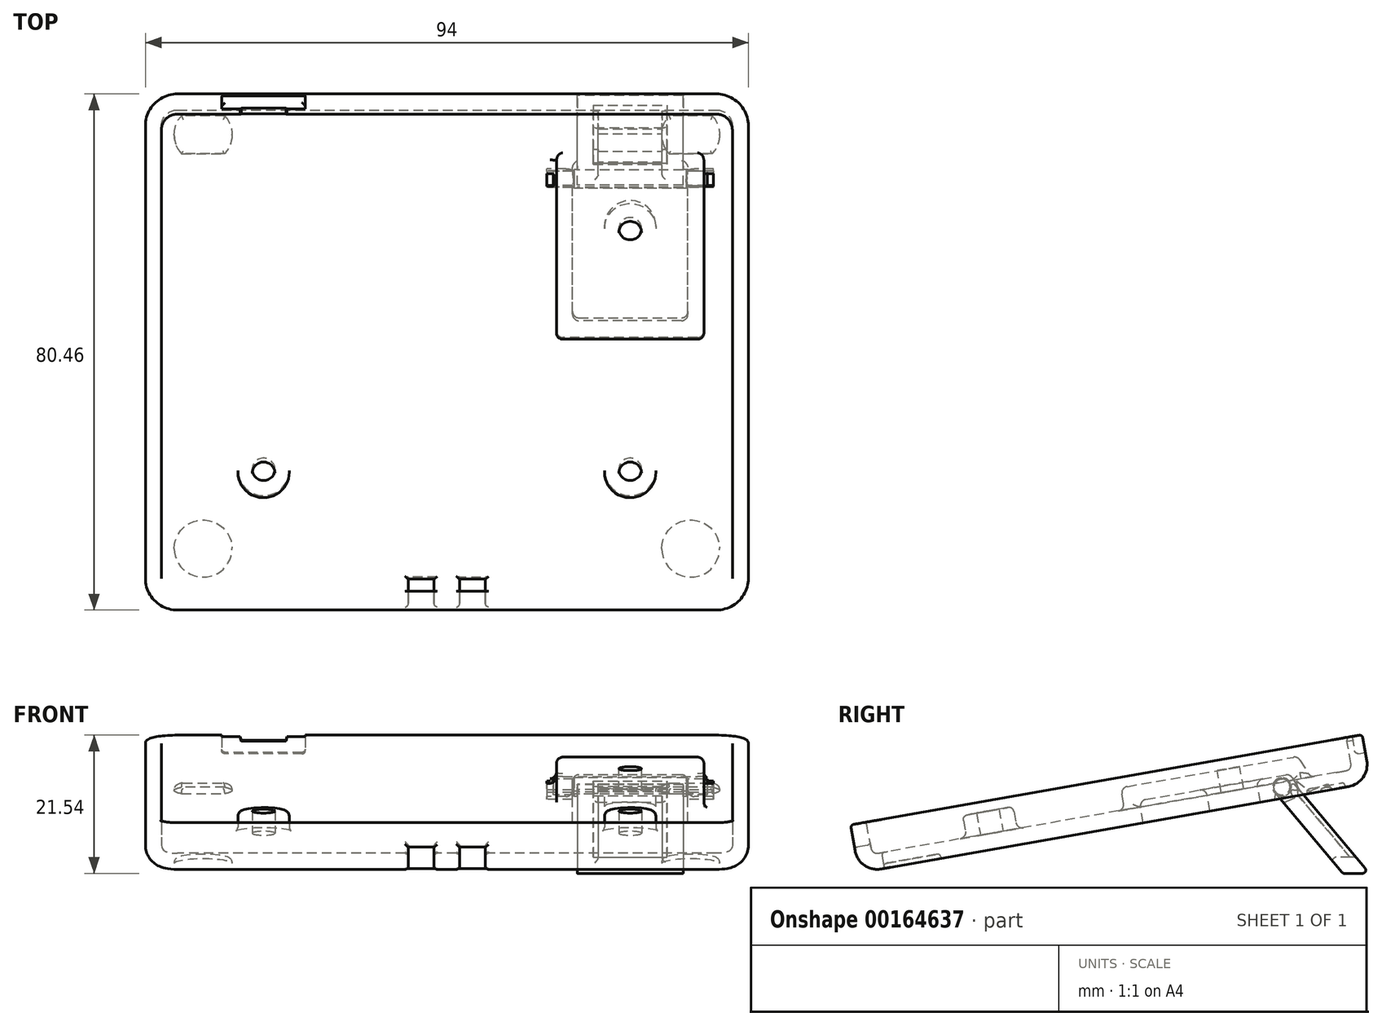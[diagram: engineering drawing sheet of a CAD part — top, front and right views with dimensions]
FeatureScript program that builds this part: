
annotation { "Feature Type Name" : "Feature", "Feature Type Description" : "" }
export const myFeature = defineFeature(function(context is Context, id is Id, definition is map)
    precondition{}
    {
        {
            var Q0;
            Q0=qCreatedBy(makeId("Top.planeOp"),FACE);
            var sketch = newSketch(context, id + "F0", { "sketchPlane" : qUnion([Q0])});
            skLineSegment(sketch, "E0.bottom", {"start": v(-47, 40.5) * mm, "end": v(47, 40.5) * mm});
            skLineSegment(sketch, "E0.top", {"start": v(-47, -40.5) * mm, "end": v(47, -40.5) * mm});
            skLineSegment(sketch, "E0.left", {"start": v(-47, 40.5) * mm, "end": v(-47, -40.5) * mm});
            skLineSegment(sketch, "E0.right", {"start": v(47, 40.5) * mm, "end": v(47, -40.5) * mm});
            skPoint(sketch, "E1", {"position": v(0, -40.5) * mm});
            skSolve(sketch);
        }
        {
            var Q0;
            Q0=qSketchRegion(id+"F0",true);
            extrude(context, id + "F1", {"entities" : qUnion([Q0]), "depth" : 7.6 * mm});
        }
        {
            var Q0;
            Q0=makeQuery(id+"F1.opExtrude","SWEPT_EDGE",EDGE,{"disambiguationData":[OSD([sQuery(id+"F0.wireOp",EDGE,"E0.top"),sQuery(id+"F0.wireOp",EDGE,"E0.left")])]});
            var Q1;
            Q1=makeQuery(id+"F1.opExtrude","SWEPT_EDGE",EDGE,{"disambiguationData":[OSD([sQuery(id+"F0.wireOp",EDGE,"E0.bottom"),sQuery(id+"F0.wireOp",EDGE,"E0.left")])]});
            var Q2;
            Q2=makeQuery(id+"F1.opExtrude","SWEPT_EDGE",EDGE,{"disambiguationData":[OSD([sQuery(id+"F0.wireOp",EDGE,"E0.top"),sQuery(id+"F0.wireOp",EDGE,"E0.right")])]});
            var Q3;
            Q3=makeQuery(id+"F1.opExtrude","SWEPT_EDGE",EDGE,{"disambiguationData":[OSD([sQuery(id+"F0.wireOp",EDGE,"E0.bottom"),sQuery(id+"F0.wireOp",EDGE,"E0.right")])]});
            fillet(context, id + "F2", {"entities" : qUnion([Q0, Q1, Q2, Q3]), "radius" : 5 * mm, "tangentPropagation" : true, "allowEdgeOverflow" : false});
        }
        {
            assignVariable(context, id + "F3", {"name" : "Thickness", "anyValue" : 2.5});
        }
        {
            var Q0;
            Q0=makeQuery(id+"F1.opExtrude","CAP_FACE",FACE,{"disambiguationData":[OSD([sQuery(id+"F0.wireOp",EDGE,"E0.bottom"),sQuery(id+"F0.wireOp",EDGE,"E0.top"),sQuery(id+"F0.wireOp",EDGE,"E0.left"),sQuery(id+"F0.wireOp",EDGE,"E0.right")])],"isStart":false});
            shell(context, id + "F4", {"entities" : qUnion([Q0]), "thickness" : (getVariable(context, 'Thickness')) * mm});
        }
        {
            var Q0;
            Q0=makeQuery(id+"F4.opShell","OFFSET_FACE",FACE,{"disambiguationData":[OSD([sQuery(id+"F0.wireOp",EDGE,"E0.bottom"),sQuery(id+"F0.wireOp",EDGE,"E0.top"),sQuery(id+"F0.wireOp",EDGE,"E0.left"),sQuery(id+"F0.wireOp",EDGE,"E0.right")])]});
            var sketch = newSketch(context, id + "F5", { "sketchPlane" : qUnion([Q0])});
            skCircle(sketch, "E2", {"center": v(-28.57, -19.05) * mm, "radius": 4 * mm});
            skCircle(sketch, "E3.0.1.0", {"center": v(-28.57, 19.05) * mm, "radius": 4 * mm, "construction": true});
            skCircle(sketch, "E3.1.0.0", {"center": v(28.58, -19.05) * mm, "radius": 4 * mm});
            skCircle(sketch, "E3.1.1.0", {"center": v(28.58, 19.05) * mm, "radius": 4 * mm, "construction": true});
            skLineSegment(sketch, "E3.direction1", {"start": v(-28.57, -19.05) * mm, "end": v(28.58, -19.05) * mm, "construction": true});
            skLineSegment(sketch, "E3.direction2", {"start": v(-28.57, -19.05) * mm, "end": v(-28.57, 19.05) * mm, "construction": true});
            skSolve(sketch);
        }
        {
            var Q0;
            Q0=qSketchRegion(id+"F5",true);
            extrude(context, id + "F6", {"entities" : qUnion([Q0]), "operationType" : NewBodyOperationType.ADD, "depth" : 3.5 * mm});
        }
        {
            var Q0;
            Q0=makeQuery(id+"F5.imprint","IMPRINT",FACE,{"disambiguationData":[TD([[makeQuery(id+"F5.imprint","IMPRINT",EDGE,{"derivedFrom":sQuery(id+"F5.wireOp",EDGE,"E2")}),-1.0]])]});
            var sketch = newSketch(context, id + "F7", { "sketchPlane" : qUnion([Q0])});
            skCircle(sketch, "E4", {"center": v(-28.57, -19.05) * mm, "radius": 1.77 * mm});
            skCircle(sketch, "E5.0.1.0", {"center": v(-28.57, 19.05) * mm, "radius": 1.77 * mm});
            skCircle(sketch, "E5.1.0.0", {"center": v(28.58, -19.05) * mm, "radius": 1.77 * mm});
            skCircle(sketch, "E5.1.1.0", {"center": v(28.58, 19.05) * mm, "radius": 1.77 * mm});
            skLineSegment(sketch, "E5.direction1", {"start": v(-28.57, -19.05) * mm, "end": v(28.58, -19.05) * mm, "construction": true});
            skLineSegment(sketch, "E5.direction2", {"start": v(-28.57, -19.05) * mm, "end": v(-28.57, 19.05) * mm, "construction": true});
            skSolve(sketch);
        }
        {
            var Q0;
            Q0=qSketchRegion(id+"F7",true);
            extrude(context, id + "F8", {"entities" : qUnion([Q0]), "operationType" : NewBodyOperationType.REMOVE, "depth" : 25 * mm});
        }
        {
            var Q0;
            Q0=makeQuery(id+"F6.opExtrude","CAP_EDGE",EDGE,{"disambiguationData":[OSD([sQuery(id+"F5.wireOp",EDGE,"E3.0.1.0")])],"isStart":false});
            var Q1;
            Q1=makeQuery(id+"F6.opExtrude","CAP_EDGE",EDGE,{"disambiguationData":[OSD([sQuery(id+"F5.wireOp",EDGE,"E2")])],"isStart":false});
            var Q2;
            Q2=makeQuery(id+"F6.opExtrude","CAP_EDGE",EDGE,{"disambiguationData":[OSD([sQuery(id+"F5.wireOp",EDGE,"E3.1.1.0")])],"isStart":false});
            var Q3;
            Q3=makeQuery(id+"F6.opExtrude","CAP_EDGE",EDGE,{"disambiguationData":[OSD([sQuery(id+"F5.wireOp",EDGE,"E3.1.0.0")])],"isStart":false});
            fillet(context, id + "F9", {"entities" : qUnion([Q0, Q1, Q2, Q3]), "radius" : 0.8 * mm, "tangentPropagation" : true, "allowEdgeOverflow" : false});
        }
        {
            var Q0;
            Q0=makeQuery(id+"F4.opShell","OFFSET_FACE",FACE,{"disambiguationData":[OSD([sQuery(id+"F0.wireOp",EDGE,"E0.bottom"),sQuery(id+"F0.wireOp",EDGE,"E0.top"),sQuery(id+"F0.wireOp",EDGE,"E0.left"),sQuery(id+"F0.wireOp",EDGE,"E0.right")])]});
            fillet(context, id + "F10", {"entities" : qUnion([Q0]), "radius" : 1 * mm, "tangentPropagation" : true, "allowEdgeOverflow" : false});
        }
        {
            var Q0;
            Q0=makeQuery(id+"F1.opExtrude","CAP_FACE",FACE,{"disambiguationData":[OSD([sQuery(id+"F0.wireOp",EDGE,"E0.bottom"),sQuery(id+"F0.wireOp",EDGE,"E0.top"),sQuery(id+"F0.wireOp",EDGE,"E0.left"),sQuery(id+"F0.wireOp",EDGE,"E0.right")])],"isStart":true});
            fillet(context, id + "F11", {"entities" : qUnion([Q0]), "radius" : 3.5 * mm, "tangentPropagation" : true, "allowEdgeOverflow" : false});
        }
        {
            var Q0;
            Q0=makeQuery(id+"F1.opExtrude","CAP_FACE",FACE,{"disambiguationData":[OSD([sQuery(id+"F0.wireOp",EDGE,"E0.bottom"),sQuery(id+"F0.wireOp",EDGE,"E0.top"),sQuery(id+"F0.wireOp",EDGE,"E0.left"),sQuery(id+"F0.wireOp",EDGE,"E0.right")])],"isStart":true});
            var sketch = newSketch(context, id + "F12", { "sketchPlane" : qUnion([Q0])});
            skLineSegment(sketch, "E6", {"start": v(0, 29.34) * mm, "end": v(0, 8.5) * mm, "construction": true});
            skCircle(sketch, "E7", {"center": v(-38, 32) * mm, "radius": 4.5 * mm});
            skCircle(sketch, "E8.MirrorC", {"center": v(38, 32) * mm, "radius": 4.5 * mm});
            skLineSegment(sketch, "E9.direction1", {"start": v(-38, 32) * mm, "end": v(-13, 32) * mm, "construction": true});
            skCircle(sketch, "E10.0.1.0", {"center": v(-38, -33.5) * mm, "radius": 4.5 * mm, "construction": true});
            skLineSegment(sketch, "E10.direction2", {"start": v(-38, 32) * mm, "end": v(-38, -33.5) * mm, "construction": true});
            skCircle(sketch, "E11.0.1.0", {"center": v(38, -32) * mm, "radius": 4.5 * mm, "construction": true});
            skLineSegment(sketch, "E11.direction1", {"start": v(38, 32) * mm, "end": v(63, 32) * mm, "construction": true});
            skLineSegment(sketch, "E11.direction2", {"start": v(38, 32) * mm, "end": v(38, -32) * mm, "construction": true});
            skLineSegment(sketch, "E12", {"start": v(-41.35, -30.5) * mm, "end": v(-34.65, -30.5) * mm});
            skLineSegment(sketch, "E13", {"start": v(-34.65, -36.5) * mm, "end": v(-41.35, -36.5) * mm});
            skLineSegment(sketch, "E14", {"start": v(-38, -33.5) * mm, "end": v(-34.31, -33.5) * mm, "construction": true});
            skArc(sketch, "E15", {"start": v(-34.65, -36.5) * mm, "mid": v(-33.5, -33.5) * mm, "end": v(-34.65, -30.5) * mm});
            skArc(sketch, "E16", {"start": v(-41.35, -30.5) * mm, "mid": v(-42.5, -33.5) * mm, "end": v(-41.35, -36.5) * mm});
            skLineSegment(sketch, "E17.1.0.0", {"start": v(41.35, -36.5) * mm, "end": v(34.65, -36.5) * mm});
            skArc(sketch, "E17.1.0.1", {"start": v(41.35, -36.5) * mm, "mid": v(42.5, -33.5) * mm, "end": v(41.35, -30.5) * mm});
            skArc(sketch, "E17.1.0.2", {"start": v(34.65, -30.5) * mm, "mid": v(33.5, -33.5) * mm, "end": v(34.65, -36.5) * mm});
            skLineSegment(sketch, "E17.1.0.3", {"start": v(34.65, -30.5) * mm, "end": v(41.35, -30.5) * mm});
            skLineSegment(sketch, "E17.direction1", {"start": v(-41.35, -36.5) * mm, "end": v(34.65, -36.5) * mm, "construction": true});
            skSolve(sketch);
        }
        {
            var Q0;
            Q0=makeQuery(id+"F1.opExtrude","CAP_FACE",FACE,{"disambiguationData":[OSD([sQuery(id+"F0.wireOp",EDGE,"E0.bottom"),sQuery(id+"F0.wireOp",EDGE,"E0.top"),sQuery(id+"F0.wireOp",EDGE,"E0.left"),sQuery(id+"F0.wireOp",EDGE,"E0.right")])],"isStart":false});
            fillet(context, id + "F13", {"entities" : qUnion([Q0]), "radius" : 0.5 * mm, "tangentPropagation" : true, "allowEdgeOverflow" : false});
        }
        {
            var Q0;
            Q0=qCreatedBy(makeId("Top.planeOp"),FACE);
            var sketch = newSketch(context, id + "F14", { "sketchPlane" : qUnion([Q0])});
            skLineSegment(sketch, "E18", {"start": v(-15.25, 0) * mm, "end": v(18.86, 0) * mm});
            skSolve(sketch);
        }
        {
            assignVariable(context, id + "F15", {"name" : "FootWidth", "anyValue" : 23});
        }
        {
            var Q0;
            Q0=qCreatedBy(makeId("Right.planeOp"),FACE);
            cPlane(context, id + "F16", {"entities" : qUnion([Q0]), "cplaneType" : CPlaneType.OFFSET, "offset" : 28.57 * mm, "width" : 150 * mm, "height" : 150 * mm});
        }
        {
            var Q0;
            Q0=qCreatedBy(id+"F16.planeOp",FACE);
            var sketch = newSketch(context, id + "F17", { "sketchPlane" : qUnion([Q0])});
            skLineSegment(sketch, "E19", {"start": v(2, 6) * mm, "end": v(30, 6) * mm});
            skLineSegment(sketch, "E20", {"start": v(30, 6) * mm, "end": v(32.42, 0) * mm});
            skLineSegment(sketch, "E21", {"start": v(32.42, 0) * mm, "end": v(2, 0) * mm});
            skLineSegment(sketch, "E22", {"start": v(2, 0) * mm, "end": v(2, 6) * mm});
            skSolve(sketch);
        }
        {
            var Q0;
            Q0=qSketchRegion(id+"F17",true);
            extrude(context, id + "F18", {"entities" : qUnion([Q0]), "operationType" : NewBodyOperationType.ADD, "endBound" : BoundingType.SYMMETRIC, "depth" : (getVariable(context, 'FootWidth')) * mm});
        }
        {
            var Q0;
            Q0=qCreatedBy(id+"F16.planeOp",FACE);
            var sketch = newSketch(context, id + "F19", { "sketchPlane" : qUnion([Q0])});
            skLineSegment(sketch, "E23.0", {"start": v(28.31, 3.5) * mm, "end": v(29.73, 0) * mm});
            skLineSegment(sketch, "E23.1", {"start": v(4.5, 3.5) * mm, "end": v(28.31, 3.5) * mm});
            skLineSegment(sketch, "E23.2", {"start": v(4.5, 0) * mm, "end": v(4.5, 3.5) * mm});
            skLineSegment(sketch, "E24", {"start": v(4.5, 0) * mm, "end": v(29.73, 0) * mm});
            skSolve(sketch);
        }
        {
            var Q0;
            Q0=qSketchRegion(id+"F19",true);
            extrude(context, id + "F20", {"entities" : qUnion([Q0]), "operationType" : NewBodyOperationType.REMOVE, "endBound" : BoundingType.SYMMETRIC, "oppositeDirection" : true, "depth" : (getVariable(context, 'FootWidth') - 2.5 * 2) * mm});
        }
        {
            var Q0;
            Q0=qSketchRegion(id+"F12",true);
            extrude(context, id + "F21", {"entities" : qUnion([Q0]), "operationType" : NewBodyOperationType.REMOVE, "oppositeDirection" : true, "depth" : 0.75 * mm});
        }
        {
            var Q0;
            Q0=makeQuery(id+"F21.boolean.opBoolean","COPY",EDGE,{"derivedFrom":makeQuery(id+"F21.opExtrude","CAP_EDGE",EDGE,{"disambiguationData":[OSD([sQuery(id+"F12.wireOp",EDGE,"E7")])],"isStart":false})});
            var Q1;
            Q1=makeQuery(id+"F21.boolean.opBoolean","COPY",EDGE,{"derivedFrom":makeQuery(id+"F21.opExtrude","CAP_EDGE",EDGE,{"disambiguationData":[OSD([sQuery(id+"F12.wireOp",EDGE,"E8.MirrorC")])],"isStart":false})});
            var Q2;
            Q2=makeQuery(id+"F21.boolean.opBoolean","COPY",EDGE,{"derivedFrom":makeQuery(id+"F21.opExtrude","CAP_EDGE",EDGE,{"disambiguationData":[OSD([sQuery(id+"F12.wireOp",EDGE,"E16")])],"isStart":false})});
            var Q3;
            Q3=makeQuery(id+"F21.boolean.opBoolean","COPY",EDGE,{"derivedFrom":makeQuery(id+"F21.opExtrude","CAP_EDGE",EDGE,{"disambiguationData":[OSD([sQuery(id+"F12.wireOp",EDGE,"E12")])],"isStart":false})});
            var Q4;
            Q4=makeQuery(id+"F21.boolean.opBoolean","COPY",EDGE,{"derivedFrom":makeQuery(id+"F21.opExtrude","CAP_EDGE",EDGE,{"disambiguationData":[OSD([sQuery(id+"F12.wireOp",EDGE,"E15")])],"isStart":false})});
            var Q5;
            Q5=makeQuery(id+"F21.boolean.opBoolean","COPY",EDGE,{"derivedFrom":makeQuery(id+"F21.opExtrude","CAP_EDGE",EDGE,{"disambiguationData":[OSD([sQuery(id+"F12.wireOp",EDGE,"E13")])],"isStart":false})});
            var Q6;
            Q6=makeQuery(id+"F21.boolean.opBoolean","COPY",EDGE,{"derivedFrom":makeQuery(id+"F21.opExtrude","CAP_EDGE",EDGE,{"disambiguationData":[OSD([sQuery(id+"F12.wireOp",EDGE,"E17.1.0.2")])],"isStart":false})});
            var Q7;
            Q7=makeQuery(id+"F21.boolean.opBoolean","COPY",EDGE,{"derivedFrom":makeQuery(id+"F21.opExtrude","CAP_EDGE",EDGE,{"disambiguationData":[OSD([sQuery(id+"F12.wireOp",EDGE,"E17.1.0.3")])],"isStart":false})});
            var Q8;
            Q8=makeQuery(id+"F21.boolean.opBoolean","COPY",EDGE,{"derivedFrom":makeQuery(id+"F21.opExtrude","CAP_EDGE",EDGE,{"disambiguationData":[OSD([sQuery(id+"F12.wireOp",EDGE,"E17.1.0.1")])],"isStart":false})});
            var Q9;
            Q9=makeQuery(id+"F21.boolean.opBoolean","COPY",EDGE,{"derivedFrom":makeQuery(id+"F21.opExtrude","CAP_EDGE",EDGE,{"disambiguationData":[OSD([sQuery(id+"F12.wireOp",EDGE,"E17.1.0.0")])],"isStart":false})});
            fillet(context, id + "F22", {"entities" : qUnion([Q0, Q1, Q2, Q3, Q4, Q5, Q6, Q7, Q8, Q9]), "radius" : 0.5 * mm, "tangentPropagation" : true, "allowEdgeOverflow" : false});
        }
        {
            var Q0;
            Q0=makeQuery(id+"F18.opExtrude","SWEPT_FACE",FACE,{"disambiguationData":[OSD([sQuery(id+"F17.wireOp",EDGE,"E19")])]});
            var sketch = newSketch(context, id + "F23", { "sketchPlane" : qUnion([Q0])});
            skCircle(sketch, "E25.0", {"center": v(28.58, 19.05) * mm, "radius": 4 * mm});
            skSolve(sketch);
        }
        {
            var Q0;
            Q0=qSketchRegion(id+"F23",true);
            var Q1;
            Q1=makeQuery(id+"F1.opExtrude","CAP_FACE",FACE,{"disambiguationData":[OSD([sQuery(id+"F0.wireOp",EDGE,"E0.bottom"),sQuery(id+"F0.wireOp",EDGE,"E0.top"),sQuery(id+"F0.wireOp",EDGE,"E0.left"),sQuery(id+"F0.wireOp",EDGE,"E0.right")])],"isStart":true});
            extrude(context, id + "F24", {"entities" : qUnion([Q0]), "operationType" : NewBodyOperationType.ADD, "endBound" : BoundingType.UP_TO_SURFACE, "oppositeDirection" : true, "endBoundEntityFace" : qUnion([Q1]), "depth" : 25 * mm});
        }
        {
            var Q0;
            Q0=makeQuery(id+"F18.opExtrude","SWEPT_FACE",FACE,{"disambiguationData":[OSD([sQuery(id+"F17.wireOp",EDGE,"E19")])]});
            var sketch = newSketch(context, id + "F25", { "sketchPlane" : qUnion([Q0])});
            skCircle(sketch, "E26.0", {"center": v(28.58, 19.05) * mm, "radius": 1.77 * mm});
            skSolve(sketch);
        }
        {
            var Q0;
            Q0=qSketchRegion(id+"F25",true);
            extrude(context, id + "F26", {"entities" : qUnion([Q0]), "operationType" : NewBodyOperationType.REMOVE, "oppositeDirection" : true, "depth" : 3.5 * mm});
        }
        {
            var Q0;
            Q0=makeQuery(id+"F24.opExtrude","TWEAK_EDGE",EDGE,{"derivedFrom":[makeQuery(id+"F1.opExtrude","CAP_FACE",FACE,{"disambiguationData":[OSD([sQuery(id+"F0.wireOp",EDGE,"E0.bottom"),sQuery(id+"F0.wireOp",EDGE,"E0.top"),sQuery(id+"F0.wireOp",EDGE,"E0.left"),sQuery(id+"F0.wireOp",EDGE,"E0.right")])],"isStart":true}),makeQuery(id+"F23.imprint","IMPRINT",EDGE,{"derivedFrom":sQuery(id+"F23.wireOp",EDGE,"E25.0")})]});
            var Q1;
            Q1=makeQuery(id+"F24.boolean.opBoolean","INTERSECT",EDGE,{"derivedFrom":[makeQuery(id+"F20.boolean.opBoolean","COPY",FACE,{"derivedFrom":makeQuery(id+"F20.opExtrude","SWEPT_FACE",FACE,{"disambiguationData":[OSD([sQuery(id+"F19.wireOp",EDGE,"E23.1")])]})}),makeQuery(id+"F24.opExtrude","SWEPT_FACE",FACE,{"disambiguationData":[OSD([sQuery(id+"F23.wireOp",EDGE,"E25.0")])]})]});
            fillet(context, id + "F27", {"entities" : qUnion([Q0, Q1]), "radius" : 1 * mm, "tangentPropagation" : true, "allowEdgeOverflow" : false});
        }
        {
            var Q0;
            Q0=makeQuery(id+"F18.opExtrude","SWEPT_EDGE",EDGE,{"disambiguationData":[OSD([sQuery(id+"F17.wireOp",EDGE,"E19"),sQuery(id+"F17.wireOp",EDGE,"E22")])]});
            var Q1;
            Q1=makeQuery(id+"F18.opExtrude","CAP_EDGE",EDGE,{"disambiguationData":[OSD([sQuery(id+"F17.wireOp",EDGE,"E19")])],"isStart":true});
            var Q2;
            Q2=makeQuery(id+"F18.opExtrude","CAP_EDGE",EDGE,{"disambiguationData":[OSD([sQuery(id+"F17.wireOp",EDGE,"E22")])],"isStart":true});
            var Q3;
            Q3=makeQuery(id+"F18.opExtrude","SWEPT_FACE",FACE,{"disambiguationData":[OSD([sQuery(id+"F17.wireOp",EDGE,"E22")])]});
            var Q4;
            {var subQ0=sQuery(id+"F0.wireOp",EDGE,"E0.right");var subQ1=sQuery(id+"F0.wireOp",EDGE,"E0.bottom");var subQ2=sQuery(id+"F0.wireOp",EDGE,"E0.left");var subQ3=sQuery(id+"F0.wireOp",EDGE,"E0.top");Q4=makeQuery(id+"F18.boolean.opBoolean","INTERSECT",EDGE,{"derivedFrom":[makeQuery(id+"FilWaYNq1lByzmx_5.boolean.opBoolean","SPLIT",FACE,{"disambiguationData":[TD([makeQuery(id+"F10.opFillet","BLEND_FACE",FACE,{"disambiguationData":[OSD([subQ3])]})])],"derivedFrom":makeQuery(id+"F4.opShell","OFFSET_FACE",FACE,{"disambiguationData":[OSD([subQ1,subQ3,subQ2,subQ0])]})}),makeQuery(id+"F18.opExtrude","CAP_FACE",FACE,{"disambiguationData":[OSD([sQuery(id+"F17.wireOp",EDGE,"E19"),sQuery(id+"F17.wireOp",EDGE,"E20"),sQuery(id+"F17.wireOp",EDGE,"E21"),sQuery(id+"F17.wireOp",EDGE,"E22")])],"isStart":true})]});}
            var Q5;
            {var subQ0=sQuery(id+"F0.wireOp",EDGE,"E0.right");var subQ1=sQuery(id+"F0.wireOp",EDGE,"E0.bottom");var subQ2=sQuery(id+"F0.wireOp",EDGE,"E0.left");var subQ3=sQuery(id+"F0.wireOp",EDGE,"E0.top");Q5=makeQuery(id+"F18.boolean.opBoolean","INTERSECT",EDGE,{"derivedFrom":[makeQuery(id+"FilWaYNq1lByzmx_5.boolean.opBoolean","SPLIT",FACE,{"disambiguationData":[TD([makeQuery(id+"F10.opFillet","BLEND_FACE",FACE,{"disambiguationData":[OSD([subQ3])]})])],"derivedFrom":makeQuery(id+"F4.opShell","OFFSET_FACE",FACE,{"disambiguationData":[OSD([subQ1,subQ3,subQ2,subQ0])]})}),makeQuery(id+"F18.opExtrude","SWEPT_FACE",FACE,{"disambiguationData":[OSD([sQuery(id+"F17.wireOp",EDGE,"E20")])]})]});}
            var Q6;
            Q6=makeQuery(id+"F18.opExtrude","CAP_EDGE",EDGE,{"disambiguationData":[OSD([sQuery(id+"F17.wireOp",EDGE,"E20")])],"isStart":true});
            var Q7;
            Q7=makeQuery(id+"F18.opExtrude","SWEPT_EDGE",EDGE,{"disambiguationData":[OSD([sQuery(id+"F17.wireOp",EDGE,"E19"),sQuery(id+"F17.wireOp",EDGE,"E20")])]});
            var Q8;
            Q8=makeQuery(id+"F18.opExtrude","CAP_EDGE",EDGE,{"disambiguationData":[OSD([sQuery(id+"F17.wireOp",EDGE,"E20")])],"isStart":false});
            var Q9;
            Q9=makeQuery(id+"F18.opExtrude","CAP_EDGE",EDGE,{"disambiguationData":[OSD([sQuery(id+"F17.wireOp",EDGE,"E19")])],"isStart":false});
            var Q10;
            Q10=makeQuery(id+"F20.boolean.opBoolean","COPY",FACE,{"derivedFrom":makeQuery(id+"F20.opExtrude","SWEPT_FACE",FACE,{"disambiguationData":[OSD([sQuery(id+"F19.wireOp",EDGE,"E23.1")])]})});
            var Q11;
            Q11=makeQuery(id+"F20.boolean.opBoolean","COPY",EDGE,{"derivedFrom":makeQuery(id+"F20.opExtrude","CAP_EDGE",EDGE,{"disambiguationData":[OSD([sQuery(id+"F19.wireOp",EDGE,"E24")])],"isStart":true})});
            var Q12;
            Q12=makeQuery(id+"F20.boolean.opBoolean","COPY",EDGE,{"derivedFrom":makeQuery(id+"F20.opExtrude","SWEPT_EDGE",EDGE,{"disambiguationData":[OSD([sQuery(id+"F19.wireOp",EDGE,"E23.2"),sQuery(id+"F19.wireOp",EDGE,"E24")])]})});
            var Q13;
            Q13=makeQuery(id+"F20.boolean.opBoolean","COPY",EDGE,{"derivedFrom":makeQuery(id+"F20.opExtrude","CAP_EDGE",EDGE,{"disambiguationData":[OSD([sQuery(id+"F19.wireOp",EDGE,"E23.2")])],"isStart":true})});
            var Q14;
            Q14=makeQuery(id+"F20.boolean.opBoolean","COPY",EDGE,{"derivedFrom":makeQuery(id+"F20.opExtrude","CAP_EDGE",EDGE,{"disambiguationData":[OSD([sQuery(id+"F19.wireOp",EDGE,"E24")])],"isStart":false})});
            var Q15;
            Q15=makeQuery(id+"F20.boolean.opBoolean","COPY",EDGE,{"derivedFrom":makeQuery(id+"F20.opExtrude","CAP_EDGE",EDGE,{"disambiguationData":[OSD([sQuery(id+"F19.wireOp",EDGE,"E23.2")])],"isStart":false})});
            var Q16;
            Q16=makeQuery(id+"F20.boolean.opBoolean","COPY",EDGE,{"derivedFrom":makeQuery(id+"F20.opExtrude","SWEPT_EDGE",EDGE,{"disambiguationData":[OSD([sQuery(id+"F19.wireOp",EDGE,"E23.0"),sQuery(id+"F19.wireOp",EDGE,"E24")])]})});
            var Q17;
            Q17=makeQuery(id+"F20.boolean.opBoolean","COPY",EDGE,{"derivedFrom":makeQuery(id+"F20.opExtrude","CAP_EDGE",EDGE,{"disambiguationData":[OSD([sQuery(id+"F19.wireOp",EDGE,"E23.0")])],"isStart":true})});
            var Q18;
            Q18=makeQuery(id+"F20.boolean.opBoolean","COPY",FACE,{"derivedFrom":makeQuery(id+"F20.opExtrude","SWEPT_FACE",FACE,{"disambiguationData":[OSD([sQuery(id+"F19.wireOp",EDGE,"E23.0")])]})});
            var Q19;
            Q19=makeQuery(id+"F9l8tkFQPLfUdVu_1.1.F20.boolean.opBoolean","COPY",EDGE,{"derivedFrom":makeQuery(id+"F9l8tkFQPLfUdVu_1.1.F20.opExtrude","SWEPT_EDGE",EDGE,{"disambiguationData":[OSD([sQuery(id+"F19.wireOp",EDGE,"E23.0"),sQuery(id+"F19.wireOp",EDGE,"E24")])]})});
            var Q20;
            Q20=makeQuery(id+"F9l8tkFQPLfUdVu_1.1.F20.boolean.opBoolean","COPY",EDGE,{"derivedFrom":makeQuery(id+"F9l8tkFQPLfUdVu_1.1.F20.opExtrude","CAP_EDGE",EDGE,{"disambiguationData":[OSD([sQuery(id+"F19.wireOp",EDGE,"E24")])],"isStart":false})});
            var Q21;
            Q21=makeQuery(id+"F9l8tkFQPLfUdVu_1.1.F20.boolean.opBoolean","COPY",EDGE,{"derivedFrom":makeQuery(id+"F9l8tkFQPLfUdVu_1.1.F20.opExtrude","SWEPT_EDGE",EDGE,{"disambiguationData":[OSD([sQuery(id+"F19.wireOp",EDGE,"E23.2"),sQuery(id+"F19.wireOp",EDGE,"E24")])]})});
            var Q22;
            Q22=makeQuery(id+"F9l8tkFQPLfUdVu_1.1.F20.boolean.opBoolean","COPY",EDGE,{"derivedFrom":makeQuery(id+"F9l8tkFQPLfUdVu_1.1.F20.opExtrude","CAP_EDGE",EDGE,{"disambiguationData":[OSD([sQuery(id+"F19.wireOp",EDGE,"E24")])],"isStart":true})});
            var Q23;
            Q23=makeQuery(id+"F9l8tkFQPLfUdVu_1.1.F20.boolean.opBoolean","COPY",EDGE,{"derivedFrom":makeQuery(id+"F9l8tkFQPLfUdVu_1.1.F20.opExtrude","CAP_EDGE",EDGE,{"disambiguationData":[OSD([sQuery(id+"F19.wireOp",EDGE,"E23.2")])],"isStart":false})});
            var Q24;
            Q24=makeQuery(id+"F9l8tkFQPLfUdVu_1.1.F20.boolean.opBoolean","COPY",EDGE,{"derivedFrom":makeQuery(id+"F9l8tkFQPLfUdVu_1.1.F20.opExtrude","CAP_EDGE",EDGE,{"disambiguationData":[OSD([sQuery(id+"F19.wireOp",EDGE,"E23.2")])],"isStart":true})});
            var Q25;
            Q25=makeQuery(id+"F9l8tkFQPLfUdVu_1.1.F20.boolean.opBoolean","COPY",EDGE,{"derivedFrom":makeQuery(id+"F9l8tkFQPLfUdVu_1.1.F20.opExtrude","CAP_EDGE",EDGE,{"disambiguationData":[OSD([sQuery(id+"F19.wireOp",EDGE,"E23.0")])],"isStart":false})});
            var Q26;
            Q26=makeQuery(id+"F9l8tkFQPLfUdVu_1.1.F20.boolean.opBoolean","COPY",EDGE,{"derivedFrom":makeQuery(id+"F9l8tkFQPLfUdVu_1.1.F20.opExtrude","CAP_EDGE",EDGE,{"disambiguationData":[OSD([sQuery(id+"F19.wireOp",EDGE,"E23.0")])],"isStart":true})});
            var Q27;
            Q27=makeQuery(id+"F9l8tkFQPLfUdVu_1.1.F18.opExtrude","SWEPT_EDGE",EDGE,{"disambiguationData":[OSD([sQuery(id+"F17.wireOp",EDGE,"E19"),sQuery(id+"F17.wireOp",EDGE,"E20")])]});
            var Q28;
            Q28=makeQuery(id+"F9l8tkFQPLfUdVu_1.1.F18.boolean.opBoolean","INTERSECT",EDGE,{"derivedFrom":[makeQuery(id+"F4.opShell","OFFSET_FACE",FACE,{"disambiguationData":[OSD([sQuery(id+"F0.wireOp",EDGE,"E0.bottom"),sQuery(id+"F0.wireOp",EDGE,"E0.top"),sQuery(id+"F0.wireOp",EDGE,"E0.left"),sQuery(id+"F0.wireOp",EDGE,"E0.right")])]}),makeQuery(id+"F9l8tkFQPLfUdVu_1.1.F18.opExtrude","SWEPT_FACE",FACE,{"disambiguationData":[OSD([sQuery(id+"F17.wireOp",EDGE,"E20")])]})]});
            var Q29;
            Q29=makeQuery(id+"F9l8tkFQPLfUdVu_1.1.F18.opExtrude","CAP_EDGE",EDGE,{"disambiguationData":[OSD([sQuery(id+"F17.wireOp",EDGE,"E20")])],"isStart":true});
            var Q30;
            Q30=makeQuery(id+"F9l8tkFQPLfUdVu_1.1.F18.boolean.opBoolean","INTERSECT",EDGE,{"derivedFrom":[makeQuery(id+"F4.opShell","OFFSET_FACE",FACE,{"disambiguationData":[OSD([sQuery(id+"F0.wireOp",EDGE,"E0.bottom"),sQuery(id+"F0.wireOp",EDGE,"E0.top"),sQuery(id+"F0.wireOp",EDGE,"E0.left"),sQuery(id+"F0.wireOp",EDGE,"E0.right")])]}),makeQuery(id+"F9l8tkFQPLfUdVu_1.1.F18.opExtrude","CAP_FACE",FACE,{"disambiguationData":[OSD([sQuery(id+"F17.wireOp",EDGE,"E19"),sQuery(id+"F17.wireOp",EDGE,"E20"),sQuery(id+"F17.wireOp",EDGE,"E21"),sQuery(id+"F17.wireOp",EDGE,"E22")])],"isStart":true})]});
            var Q31;
            Q31=makeQuery(id+"F9l8tkFQPLfUdVu_1.1.F18.opExtrude","CAP_EDGE",EDGE,{"disambiguationData":[OSD([sQuery(id+"F17.wireOp",EDGE,"E19")])],"isStart":true});
            var Q32;
            Q32=makeQuery(id+"F9l8tkFQPLfUdVu_1.1.F18.opExtrude","CAP_EDGE",EDGE,{"disambiguationData":[OSD([sQuery(id+"F17.wireOp",EDGE,"E20")])],"isStart":false});
            var Q33;
            Q33=makeQuery(id+"F9l8tkFQPLfUdVu_1.1.F18.boolean.opBoolean","INTERSECT",EDGE,{"derivedFrom":[makeQuery(id+"F4.opShell","OFFSET_FACE",FACE,{"disambiguationData":[OSD([sQuery(id+"F0.wireOp",EDGE,"E0.bottom"),sQuery(id+"F0.wireOp",EDGE,"E0.top"),sQuery(id+"F0.wireOp",EDGE,"E0.left"),sQuery(id+"F0.wireOp",EDGE,"E0.right")])]}),makeQuery(id+"F9l8tkFQPLfUdVu_1.1.F18.opExtrude","CAP_FACE",FACE,{"disambiguationData":[OSD([sQuery(id+"F17.wireOp",EDGE,"E19"),sQuery(id+"F17.wireOp",EDGE,"E20"),sQuery(id+"F17.wireOp",EDGE,"E21"),sQuery(id+"F17.wireOp",EDGE,"E22")])],"isStart":false})]});
            var Q34;
            Q34=makeQuery(id+"F9l8tkFQPLfUdVu_1.1.F18.opExtrude","CAP_EDGE",EDGE,{"disambiguationData":[OSD([sQuery(id+"F17.wireOp",EDGE,"E19")])],"isStart":false});
            var Q35;
            Q35=makeQuery(id+"F9l8tkFQPLfUdVu_1.1.F18.opExtrude","SWEPT_EDGE",EDGE,{"disambiguationData":[OSD([sQuery(id+"F17.wireOp",EDGE,"E19"),sQuery(id+"F17.wireOp",EDGE,"E22")])]});
            var Q36;
            Q36=makeQuery(id+"F9l8tkFQPLfUdVu_1.1.F18.boolean.opBoolean","INTERSECT",EDGE,{"derivedFrom":[makeQuery(id+"F4.opShell","OFFSET_FACE",FACE,{"disambiguationData":[OSD([sQuery(id+"F0.wireOp",EDGE,"E0.bottom"),sQuery(id+"F0.wireOp",EDGE,"E0.top"),sQuery(id+"F0.wireOp",EDGE,"E0.left"),sQuery(id+"F0.wireOp",EDGE,"E0.right")])]}),makeQuery(id+"F9l8tkFQPLfUdVu_1.1.F18.opExtrude","SWEPT_FACE",FACE,{"disambiguationData":[OSD([sQuery(id+"F17.wireOp",EDGE,"E22")])]})]});
            var Q37;
            Q37=makeQuery(id+"F9l8tkFQPLfUdVu_1.1.F18.opExtrude","CAP_EDGE",EDGE,{"disambiguationData":[OSD([sQuery(id+"F17.wireOp",EDGE,"E22")])],"isStart":false});
            var Q38;
            Q38=makeQuery(id+"F9l8tkFQPLfUdVu_1.1.F18.opExtrude","CAP_EDGE",EDGE,{"disambiguationData":[OSD([sQuery(id+"F17.wireOp",EDGE,"E22")])],"isStart":true});
            var Q39;
            Q39=makeQuery(id+"F9l8tkFQPLfUdVu_1.1.F20.boolean.opBoolean","COPY",EDGE,{"derivedFrom":makeQuery(id+"F9l8tkFQPLfUdVu_1.1.F20.opExtrude","SWEPT_EDGE",EDGE,{"disambiguationData":[OSD([sQuery(id+"F19.wireOp",EDGE,"E23.1"),sQuery(id+"F19.wireOp",EDGE,"E23.2")])]})});
            var Q40;
            Q40=makeQuery(id+"F9l8tkFQPLfUdVu_1.1.F20.boolean.opBoolean","COPY",EDGE,{"derivedFrom":makeQuery(id+"F9l8tkFQPLfUdVu_1.1.F20.opExtrude","CAP_EDGE",EDGE,{"disambiguationData":[OSD([sQuery(id+"F19.wireOp",EDGE,"E23.1")])],"isStart":false})});
            var Q41;
            Q41=makeQuery(id+"F9l8tkFQPLfUdVu_1.1.F20.boolean.opBoolean","COPY",EDGE,{"derivedFrom":makeQuery(id+"F9l8tkFQPLfUdVu_1.1.F20.opExtrude","CAP_EDGE",EDGE,{"disambiguationData":[OSD([sQuery(id+"F19.wireOp",EDGE,"E23.1")])],"isStart":true})});
            var Q42;
            Q42=makeQuery(id+"F9l8tkFQPLfUdVu_1.1.F20.boolean.opBoolean","COPY",FACE,{"derivedFrom":makeQuery(id+"F9l8tkFQPLfUdVu_1.1.F20.opExtrude","SWEPT_FACE",FACE,{"disambiguationData":[OSD([sQuery(id+"F19.wireOp",EDGE,"E23.0")])]})});
            fillet(context, id + "F28", {"entities" : qUnion([Q0, Q1, Q2, Q3, Q4, Q5, Q6, Q7, Q8, Q9, Q10, Q11, Q12, Q13, Q14, Q15, Q16, Q17, Q18, Q19, Q20, Q21, Q22, Q23, Q24, Q25, Q26, Q27, Q28, Q29, Q30, Q31, Q32, Q33, Q34, Q35, Q36, Q37, Q38, Q39, Q40, Q41, Q42]), "radius" : 1 * mm, "tangentPropagation" : true, "allowEdgeOverflow" : false});
        }
        {
            var Q0;
            Q0=qCreatedBy(id+"F16.planeOp",FACE);
            var sketch = newSketch(context, id + "F29", { "sketchPlane" : qUnion([Q0])});
            skArc(sketch, "E27", {"start": v(27.97, 1.25) * mm, "mid": v(26.75, 3) * mm, "end": v(25.53, 1.25) * mm});
            skLineSegment(sketch, "E28", {"start": v(25.4, 0) * mm, "end": v(28.1, 0) * mm});
            skLineSegment(sketch, "E29", {"start": v(25.53, 1.25) * mm, "end": v(25.6, 1.06) * mm});
            skLineSegment(sketch, "E30", {"start": v(25.6, 1.06) * mm, "end": v(25.4, 0) * mm});
            skLineSegment(sketch, "E31", {"start": v(27.97, 1.25) * mm, "end": v(27.9, 1.06) * mm});
            skLineSegment(sketch, "E32", {"start": v(27.9, 1.06) * mm, "end": v(28.1, 0) * mm});
            skLineSegment(sketch, "E33", {"start": v(26.75, 1.7) * mm, "end": v(26.75, 0.9) * mm, "construction": true});
            skPoint(sketch, "E34.0", {"position": v(2, 0) * mm});
            skSolve(sketch);
        }
        {
            var Q0;
            Q0=qSketchRegion(id+"F29",true);
            extrude(context, id + "F30", {"entities" : qUnion([Q0]), "operationType" : NewBodyOperationType.REMOVE, "endBound" : BoundingType.SYMMETRIC, "depth" : (getVariable(context, 'FootWidth') + 3) * mm});
        }
        {
            var Q0;
            Q0=makeQuery(id+"F1.opExtrude","SWEPT_BODY",BODY,{"disambiguationData":[OSD([sQuery(id+"F0.wireOp",EDGE,"E0.bottom"),sQuery(id+"F0.wireOp",EDGE,"E0.top"),sQuery(id+"F0.wireOp",EDGE,"E0.left"),sQuery(id+"F0.wireOp",EDGE,"E0.right")])]});
            var Q1;
            Q1=makeQuery(id+"FEbTksUdMywidjK_1.opExtrude","SWEPT_BODY",BODY,{"disambiguationData":[OSD([sQuery(id+"FKX2OaeCSXbjlxv_1.wireOp",EDGE,"g9NftOec-wNn0-Jsp5-IVkA-v6Q9gR38QLaD.bottom"),sQuery(id+"FKX2OaeCSXbjlxv_1.wireOp",EDGE,"g9NftOec-wNn0-Jsp5-IVkA-v6Q9gR38QLaD.top"),sQuery(id+"FKX2OaeCSXbjlxv_1.wireOp",EDGE,"g9NftOec-wNn0-Jsp5-IVkA-v6Q9gR38QLaD.left"),sQuery(id+"FKX2OaeCSXbjlxv_1.wireOp",EDGE,"g9NftOec-wNn0-Jsp5-IVkA-v6Q9gR38QLaD.right")])]});
            var Q2;
            Q2=makeQuery(id+"FLwaovvO8MrASWp_2.merge.F51wT92JSOcFrXW_23.opExtrude","SWEPT_BODY",BODY,{"disambiguationData":[OSD([sQuery(id+"FLwaovvO8MrASWp_2.merge.FVQRNRXO9YIzRv7_23.wireOp",EDGE,"90ddd970-3579-4ef8-be16-2660a2f9e075.bottom"),sQuery(id+"FLwaovvO8MrASWp_2.merge.FVQRNRXO9YIzRv7_23.wireOp",EDGE,"90ddd970-3579-4ef8-be16-2660a2f9e075.top"),sQuery(id+"FLwaovvO8MrASWp_2.merge.FVQRNRXO9YIzRv7_23.wireOp",EDGE,"90ddd970-3579-4ef8-be16-2660a2f9e075.left"),sQuery(id+"FLwaovvO8MrASWp_2.merge.FVQRNRXO9YIzRv7_23.wireOp",EDGE,"90ddd970-3579-4ef8-be16-2660a2f9e075.right")])]});
            var Q3;
            Q3=makeQuery(id+"Fj0Eu8bYN3sUu6t_3.opExtrude","SWEPT_BODY",BODY,{"disambiguationData":[OSD([sQuery(id+"F7yx7wkMNnjRKGf_3.wireOp",EDGE,"eeb5266b-afda-4c11-85dd-e03b1d8f963a.0"),sQuery(id+"F7yx7wkMNnjRKGf_3.wireOp",EDGE,"eeb5266b-afda-4c11-85dd-e03b1d8f963a.1"),sQuery(id+"F7yx7wkMNnjRKGf_3.wireOp",EDGE,"eeb5266b-afda-4c11-85dd-e03b1d8f963a.2"),sQuery(id+"F7yx7wkMNnjRKGf_3.wireOp",EDGE,"Sjp20wkr-GL0I-67mY-yOA2-zPCHcegtjmW0"),sQuery(id+"F7yx7wkMNnjRKGf_3.wireOp",EDGE,"7VOQmwQP-byOQ-jfAL-egTg-MQnNcLXBwj0H"),sQuery(id+"F7yx7wkMNnjRKGf_3.wireOp",EDGE,"losnIXg9-lelz-Dvec-CEj2-Y1hkcEEa8RQi"),sQuery(id+"F7yx7wkMNnjRKGf_3.wireOp",EDGE,"QwOmv3CZ-eYIC-Wnk4-euwr-VTdzEUVm5c8k"),sQuery(id+"F7yx7wkMNnjRKGf_3.wireOp",EDGE,"nJwuLorS-p07x-P2mC-5KsE-xesRUc9gh4jH"),sQuery(id+"F7yx7wkMNnjRKGf_3.wireOp",EDGE,"TYMp9W4P-0IKO-KKH6-4iec-fhLdNv4Jpbul")])]});
            var Q4;
            Q4=makeQuery(id+"F9e8veecUQ0AhO2_4.opExtrude","SWEPT_BODY",BODY,{"disambiguationData":[OSD([sQuery(id+"FxhmBhLSTdEBXH4_4.wireOp",EDGE,"sbWJf8b4-muHd-ZDzS-Xi0M-BkMlyJhnCTyb.bottom"),sQuery(id+"FxhmBhLSTdEBXH4_4.wireOp",EDGE,"sbWJf8b4-muHd-ZDzS-Xi0M-BkMlyJhnCTyb.top"),sQuery(id+"FxhmBhLSTdEBXH4_4.wireOp",EDGE,"sbWJf8b4-muHd-ZDzS-Xi0M-BkMlyJhnCTyb.left"),sQuery(id+"FxhmBhLSTdEBXH4_4.wireOp",EDGE,"sbWJf8b4-muHd-ZDzS-Xi0M-BkMlyJhnCTyb.right")])]});
            var Q5;
            Q5=sQuery(id+"F14.wireOp",EDGE,"E18");
            transform(context, id + "F31", {"entities" : qUnion([Q0, Q1, Q2, Q3, Q4]), "transformType" : TransformType.ROTATION, "transformAxis" : qUnion([Q5]), "angle" : 10 * degree, "makeCopy" : false});
        }
        {
            var Q0;
            Q0=qCreatedBy(id+"F16.planeOp",FACE);
            var sketch = newSketch(context, id + "F32", { "sketchPlane" : qUnion([Q0])});
            skLineSegment(sketch, "E35", {"start": v(-33.48, -7.1) * mm, "end": v(29.13, -7.1) * mm, "construction": true});
            skLineSegment(sketch, "E36", {"start": v(29.13, -7.1) * mm, "end": v(29.13, 7.53) * mm, "construction": true});
            skLineSegment(sketch, "E37", {"start": v(24.85, 6.03) * mm, "end": v(27.26, 6.69) * mm});
            skCircle(sketch, "E38", {"center": v(26.05, 6.36) * mm, "radius": 1.25 * mm, "construction": true});
            skLineSegment(sketch, "E39.0", {"start": v(-27.7, -4.12) * mm, "end": v(-35.58, -5.51) * mm, "construction": true});
            skLineSegment(sketch, "E40.0", {"start": v(-27.36, -6.1) * mm, "end": v(-35.24, -7.48) * mm, "construction": true});
            skLineSegment(sketch, "E41", {"start": v(24.53, 5.94) * mm, "end": v(35.53, -7.1) * mm});
            skLineSegment(sketch, "E42", {"start": v(27.91, 6.87) * mm, "end": v(39.7, -7.1) * mm});
            skLineSegment(sketch, "E43", {"start": v(24.53, 5.94) * mm, "end": v(24.85, 6.03) * mm});
            skLineSegment(sketch, "E44", {"start": v(27.91, 6.87) * mm, "end": v(27.26, 6.69) * mm});
            skLineSegment(sketch, "E45", {"start": v(39.7, -7.1) * mm, "end": v(35.53, -7.1) * mm});
            skArc(sketch, "E46.0", {"start": v(28.3, 7.6) * mm, "mid": v(28.41, 7.4) * mm, "end": v(28.5, 7.2) * mm});
            skSolve(sketch);
        }
        {
            var Q0;
            Q0=qSketchRegion(id+"F32",true);
            extrude(context, id + "F33", {"entities" : qUnion([Q0]), "endBound" : BoundingType.SYMMETRIC, "depth" : 16.5 * mm});
        }
        {
            var Q0;
            Q0=qCreatedBy(id+"F16.planeOp",FACE);
            var sketch = newSketch(context, id + "F34", { "sketchPlane" : qUnion([Q0])});
            skCircle(sketch, "E47.0", {"center": v(26.05, 6.36) * mm, "radius": 1.25 * mm});
            skSolve(sketch);
        }
        {
            var Q0;
            Q0=qSketchRegion(id+"F34",true);
            extrude(context, id + "F35", {"entities" : qUnion([Q0]), "operationType" : NewBodyOperationType.ADD, "endBound" : BoundingType.SYMMETRIC, "depth" : 24 * mm});
        }
        {
            var Q0;
            Q0=qCreatedBy(id+"F16.planeOp",FACE);
            var sketch = newSketch(context, id + "F36", { "sketchPlane" : qUnion([Q0])});
            skCircle(sketch, "E48.0", {"center": v(26.05, 6.36) * mm, "radius": 1.45 * mm});
            skSolve(sketch);
        }
        {
            var Q0;
            Q0=qSketchRegion(id+"F36",true);
            extrude(context, id + "F37", {"entities" : qUnion([Q0]), "operationType" : NewBodyOperationType.ADD, "endBound" : BoundingType.SYMMETRIC, "depth" : 17.5 * mm});
        }
        {
            var Q0;
            Q0=qCreatedBy(id+"F16.planeOp",FACE);
            var sketch = newSketch(context, id + "F38", { "sketchPlane" : qUnion([Q0])});
            skLineSegment(sketch, "E49", {"start": v(43.2, -4.6) * mm, "end": v(36.69, -4.6) * mm});
            skLineSegment(sketch, "E50", {"start": v(36.69, -4.6) * mm, "end": v(28.6, 4.98) * mm});
            skLineSegment(sketch, "E51", {"start": v(28.6, 4.98) * mm, "end": v(28.38, 7.26) * mm});
            skLineSegment(sketch, "E52", {"start": v(28.38, 7.26) * mm, "end": v(43.2, -4.6) * mm});
            skSolve(sketch);
        }
        {
            var Q0;
            Q0=qSketchRegion(id+"F38",true);
            extrude(context, id + "F39", {"entities" : qUnion([Q0]), "operationType" : NewBodyOperationType.REMOVE, "endBound" : BoundingType.SYMMETRIC, "oppositeDirection" : true, "depth" : (16.5 - 2.5 * 2) * mm});
        }
        {
            var Q0;
            Q0=qCreatedBy(makeId("Top.planeOp"),FACE);
            var Q1;
            Q1=sQuery(id+"F32.wireOp",VERTEX,"E38.center");
            cPlane(context, id + "F40", {"entities" : qUnion([Q0, Q1]), "cplaneType" : CPlaneType.PLANE_POINT, "offset" : 7 * mm, "width" : 150 * mm, "height" : 150 * mm});
        }
        {
            var Q0;
            Q0=qCreatedBy(id+"F40.planeOp",FACE);
            var sketch = newSketch(context, id + "F41", { "sketchPlane" : qUnion([Q0])});
            skLineSegment(sketch, "E53", {"start": v(12.14, 26.05) * mm, "end": v(28.07, 26.05) * mm});
            skSolve(sketch);
        }
        {
            var Q0;
            Q0=qCreatedBy(id+"F16.planeOp",FACE);
            var sketch = newSketch(context, id + "F42", { "sketchPlane" : qUnion([Q0])});
            skLineSegment(sketch, "E54", {"start": v(43.16, -4.6) * mm, "end": v(33.32, -4.6) * mm});
            skLineSegment(sketch, "E55", {"start": v(33.32, -4.6) * mm, "end": v(25.32, 3.5) * mm});
            skLineSegment(sketch, "E56", {"start": v(25.32, 3.5) * mm, "end": v(33.1, 6.87) * mm});
            skLineSegment(sketch, "E57", {"start": v(33.1, 6.87) * mm, "end": v(43.16, -4.6) * mm});
            skSolve(sketch);
        }
        {
            var Q0;
            Q0=qSketchRegion(id+"F42",true);
            extrude(context, id + "F43", {"entities" : qUnion([Q0]), "operationType" : NewBodyOperationType.REMOVE, "endBound" : BoundingType.SYMMETRIC, "oppositeDirection" : true, "depth" : 10 * mm});
        }
        {
            var Q0;
            Q0=makeQuery(id+"F33.opExtrude","SWEPT_EDGE",EDGE,{"disambiguationData":[OSD([sQuery(id+"F32.wireOp",EDGE,"E42"),sQuery(id+"F32.wireOp",EDGE,"lMs646Tl-KVh7-EVDn-IebO-JsbN2g6ax7Xg")])]});
            var Q1;
            Q1=makeQuery(id+"F33.opExtrude","SWEPT_EDGE",EDGE,{"disambiguationData":[OSD([sQuery(id+"F32.wireOp",EDGE,"E41"),sQuery(id+"F32.wireOp",EDGE,"NX3cYOfe-ebx6-K3RK-W4n3-XHnWPqz6DOJI")])]});
            var Q2;
            Q2=makeQuery(id+"F43.boolean.opBoolean","INTERSECT",EDGE,{"derivedFrom":[makeQuery(id+"F33.opExtrude","SWEPT_FACE",FACE,{"disambiguationData":[OSD([sQuery(id+"F32.wireOp",EDGE,"E41")])]}),makeQuery(id+"F43.opExtrude","SWEPT_FACE",FACE,{"disambiguationData":[OSD([sQuery(id+"F42.wireOp",EDGE,"E54")])]})]});
            var Q3;
            Q3=makeQuery(id+"F43.boolean.opBoolean","INTERSECT",EDGE,{"derivedFrom":[makeQuery(id+"F33.opExtrude","SWEPT_FACE",FACE,{"disambiguationData":[OSD([sQuery(id+"F32.wireOp",EDGE,"E41")])]}),makeQuery(id+"F43.opExtrude","CAP_FACE",FACE,{"disambiguationData":[OSD([sQuery(id+"F42.wireOp",EDGE,"E54"),sQuery(id+"F42.wireOp",EDGE,"E55"),sQuery(id+"F42.wireOp",EDGE,"E56"),sQuery(id+"F42.wireOp",EDGE,"E57")])],"isStart":false})]});
            var Q4;
            Q4=makeQuery(id+"F43.boolean.opBoolean","INTERSECT",EDGE,{"derivedFrom":[makeQuery(id+"F33.opExtrude","SWEPT_FACE",FACE,{"disambiguationData":[OSD([sQuery(id+"F32.wireOp",EDGE,"E41")])]}),makeQuery(id+"F43.opExtrude","SWEPT_FACE",FACE,{"disambiguationData":[OSD([sQuery(id+"F42.wireOp",EDGE,"E56")])]})]});
            var Q5;
            Q5=makeQuery(id+"F43.boolean.opBoolean","INTERSECT",EDGE,{"derivedFrom":[makeQuery(id+"F33.opExtrude","SWEPT_FACE",FACE,{"disambiguationData":[OSD([sQuery(id+"F32.wireOp",EDGE,"E41")])]}),makeQuery(id+"F43.opExtrude","CAP_FACE",FACE,{"disambiguationData":[OSD([sQuery(id+"F42.wireOp",EDGE,"E54"),sQuery(id+"F42.wireOp",EDGE,"E55"),sQuery(id+"F42.wireOp",EDGE,"E56"),sQuery(id+"F42.wireOp",EDGE,"E57")])],"isStart":true})]});
            fillet(context, id + "F44", {"entities" : qUnion([Q0, Q1, Q2, Q3, Q4, Q5]), "radius" : 0.5 * mm, "tangentPropagation" : true, "allowEdgeOverflow" : false});
        }
        {
            var Q0;
            Q0=makeQuery(id+"F1.opExtrude","CAP_FACE",FACE,{"disambiguationData":[OSD([sQuery(id+"F0.wireOp",EDGE,"E0.bottom"),sQuery(id+"F0.wireOp",EDGE,"E0.top"),sQuery(id+"F0.wireOp",EDGE,"E0.left"),sQuery(id+"F0.wireOp",EDGE,"E0.right")])],"isStart":true});
            var sketch = newSketch(context, id + "F45", { "sketchPlane" : qUnion([Q0])});
            skLineSegment(sketch, "E58", {"start": v(0, 23.73) * mm, "end": v(0, 50.2) * mm});
            skPoint(sketch, "E58.endSnap0", {"position": v(0, 37) * mm});
            skLineSegment(sketch, "E59.bottom", {"start": v(-2, 36.5) * mm, "end": v(-6, 36.5) * mm});
            skLineSegment(sketch, "E59.top", {"start": v(-2, 41) * mm, "end": v(-6, 41) * mm});
            skLineSegment(sketch, "E59.left", {"start": v(-2, 36.5) * mm, "end": v(-2, 41) * mm});
            skLineSegment(sketch, "E59.right", {"start": v(-6, 36.5) * mm, "end": v(-6, 41) * mm});
            skLineSegment(sketch, "E60.MirrorCS", {"start": v(2, 41) * mm, "end": v(6, 41) * mm});
            skLineSegment(sketch, "E61.MirrorCS", {"start": v(2, 36.5) * mm, "end": v(2, 41) * mm});
            skLineSegment(sketch, "E62.MirrorCS", {"start": v(2, 36.5) * mm, "end": v(6, 36.5) * mm});
            skLineSegment(sketch, "E63.MirrorCS", {"start": v(6, 36.5) * mm, "end": v(6, 41) * mm});
            skSolve(sketch);
        }
        {
            var Q0;
            Q0=qSketchRegion(id+"F45",true);
            extrude(context, id + "F46", {"entities" : qUnion([Q0]), "operationType" : NewBodyOperationType.REMOVE, "oppositeDirection" : true, "depth" : 4 * mm});
        }
        {
            var Q0;
            Q0=makeQuery(id+"F46.boolean.opBoolean","COPY",EDGE,{"derivedFrom":makeQuery(id+"F46.opExtrude","CAP_EDGE",EDGE,{"disambiguationData":[OSD([sQuery(id+"F45.wireOp",EDGE,"E62.MirrorCS")])],"isStart":true})});
            var Q1;
            Q1=makeQuery(id+"F46.boolean.opBoolean","INTERSECT",EDGE,{"derivedFrom":[makeQuery(id+"F11.opFillet","BLEND_FACE",FACE,{"disambiguationData":[OSD([sQuery(id+"F0.wireOp",EDGE,"E0.top")])]}),makeQuery(id+"F46.opExtrude","SWEPT_FACE",FACE,{"disambiguationData":[OSD([sQuery(id+"F45.wireOp",EDGE,"E61.MirrorCS")])]})]});
            var Q2;
            Q2=makeQuery(id+"F46.boolean.opBoolean","INTERSECT",EDGE,{"derivedFrom":[makeQuery(id+"F1.opExtrude","SWEPT_FACE",FACE,{"disambiguationData":[OSD([sQuery(id+"F0.wireOp",EDGE,"E0.top")])]}),makeQuery(id+"F46.opExtrude","CAP_FACE",FACE,{"disambiguationData":[OSD([sQuery(id+"F45.wireOp",EDGE,"E60.MirrorCS"),sQuery(id+"F45.wireOp",EDGE,"E61.MirrorCS"),sQuery(id+"F45.wireOp",EDGE,"E62.MirrorCS"),sQuery(id+"F45.wireOp",EDGE,"E63.MirrorCS")])],"isStart":false})]});
            var Q3;
            Q3=makeQuery(id+"F46.boolean.opBoolean","INTERSECT",EDGE,{"derivedFrom":[makeQuery(id+"F11.opFillet","BLEND_FACE",FACE,{"disambiguationData":[OSD([sQuery(id+"F0.wireOp",EDGE,"E0.top")])]}),makeQuery(id+"F46.opExtrude","SWEPT_FACE",FACE,{"disambiguationData":[OSD([sQuery(id+"F45.wireOp",EDGE,"E63.MirrorCS")])]})]});
            var Q4;
            Q4=makeQuery(id+"F46.boolean.opBoolean","COPY",EDGE,{"derivedFrom":makeQuery(id+"F46.opExtrude","CAP_EDGE",EDGE,{"disambiguationData":[OSD([sQuery(id+"F45.wireOp",EDGE,"E59.bottom")])],"isStart":true})});
            var Q5;
            Q5=makeQuery(id+"F46.boolean.opBoolean","INTERSECT",EDGE,{"derivedFrom":[makeQuery(id+"F11.opFillet","BLEND_FACE",FACE,{"disambiguationData":[OSD([sQuery(id+"F0.wireOp",EDGE,"E0.top")])]}),makeQuery(id+"F46.opExtrude","SWEPT_FACE",FACE,{"disambiguationData":[OSD([sQuery(id+"F45.wireOp",EDGE,"E59.left")])]})]});
            var Q6;
            Q6=makeQuery(id+"F46.boolean.opBoolean","INTERSECT",EDGE,{"derivedFrom":[makeQuery(id+"F11.opFillet","BLEND_FACE",FACE,{"disambiguationData":[OSD([sQuery(id+"F0.wireOp",EDGE,"E0.top")])]}),makeQuery(id+"F46.opExtrude","SWEPT_FACE",FACE,{"disambiguationData":[OSD([sQuery(id+"F45.wireOp",EDGE,"E59.right")])]})]});
            var Q7;
            Q7=makeQuery(id+"F46.boolean.opBoolean","INTERSECT",EDGE,{"derivedFrom":[makeQuery(id+"F1.opExtrude","SWEPT_FACE",FACE,{"disambiguationData":[OSD([sQuery(id+"F0.wireOp",EDGE,"E0.top")])]}),makeQuery(id+"F46.opExtrude","CAP_FACE",FACE,{"disambiguationData":[OSD([sQuery(id+"F45.wireOp",EDGE,"E59.bottom"),sQuery(id+"F45.wireOp",EDGE,"E59.top"),sQuery(id+"F45.wireOp",EDGE,"E59.left"),sQuery(id+"F45.wireOp",EDGE,"E59.right")])],"isStart":false})]});
            var Q8;
            {var subQ0=sQuery(id+"F0.wireOp",EDGE,"E0.bottom");var subQ1=sQuery(id+"F0.wireOp",EDGE,"E0.right");var subQ2=sQuery(id+"F0.wireOp",EDGE,"E0.left");var subQ3=sQuery(id+"F0.wireOp",EDGE,"E0.top");Q8=makeQuery(id+"F46.boolean.opBoolean","INTERSECT",EDGE,{"derivedFrom":[makeQuery(id+"FilWaYNq1lByzmx_5.boolean.opBoolean","SPLIT",FACE,{"disambiguationData":[TD([makeQuery(id+"F10.opFillet","BLEND_FACE",FACE,{"disambiguationData":[OSD([subQ3])]})])],"derivedFrom":makeQuery(id+"F4.opShell","OFFSET_FACE",FACE,{"disambiguationData":[OSD([subQ0,subQ3,subQ2,subQ1])]})}),makeQuery(id+"F46.opExtrude","SWEPT_FACE",FACE,{"disambiguationData":[OSD([sQuery(id+"F45.wireOp",EDGE,"E59.bottom")])]})]});}
            var Q9;
            Q9=makeQuery(id+"F46.boolean.opBoolean","INTERSECT",EDGE,{"derivedFrom":[makeQuery(id+"F10.opFillet","BLEND_FACE",FACE,{"disambiguationData":[OSD([sQuery(id+"F0.wireOp",EDGE,"E0.top")])]}),makeQuery(id+"F46.opExtrude","SWEPT_FACE",FACE,{"disambiguationData":[OSD([sQuery(id+"F45.wireOp",EDGE,"E59.right")])]})]});
            var Q10;
            Q10=makeQuery(id+"F46.boolean.opBoolean","INTERSECT",EDGE,{"derivedFrom":[makeQuery(id+"F10.opFillet","BLEND_FACE",FACE,{"disambiguationData":[OSD([sQuery(id+"F0.wireOp",EDGE,"E0.top")])]}),makeQuery(id+"F46.opExtrude","SWEPT_FACE",FACE,{"disambiguationData":[OSD([sQuery(id+"F45.wireOp",EDGE,"E59.left")])]})]});
            var Q11;
            Q11=makeQuery(id+"F46.boolean.opBoolean","INTERSECT",EDGE,{"derivedFrom":[makeQuery(id+"F4.opShell","OFFSET_FACE",FACE,{"disambiguationData":[OSD([sQuery(id+"F0.wireOp",EDGE,"E0.top")])]}),makeQuery(id+"F46.opExtrude","CAP_FACE",FACE,{"disambiguationData":[OSD([sQuery(id+"F45.wireOp",EDGE,"E59.bottom"),sQuery(id+"F45.wireOp",EDGE,"E59.top"),sQuery(id+"F45.wireOp",EDGE,"E59.left"),sQuery(id+"F45.wireOp",EDGE,"E59.right")])],"isStart":false})]});
            var Q12;
            {var subQ0=sQuery(id+"F0.wireOp",EDGE,"E0.bottom");var subQ1=sQuery(id+"F0.wireOp",EDGE,"E0.right");var subQ2=sQuery(id+"F0.wireOp",EDGE,"E0.left");var subQ3=sQuery(id+"F0.wireOp",EDGE,"E0.top");Q12=makeQuery(id+"F46.boolean.opBoolean","INTERSECT",EDGE,{"derivedFrom":[makeQuery(id+"FilWaYNq1lByzmx_5.boolean.opBoolean","SPLIT",FACE,{"disambiguationData":[TD([makeQuery(id+"F10.opFillet","BLEND_FACE",FACE,{"disambiguationData":[OSD([subQ3])]})])],"derivedFrom":makeQuery(id+"F4.opShell","OFFSET_FACE",FACE,{"disambiguationData":[OSD([subQ0,subQ3,subQ2,subQ1])]})}),makeQuery(id+"F46.opExtrude","SWEPT_FACE",FACE,{"disambiguationData":[OSD([sQuery(id+"F45.wireOp",EDGE,"E62.MirrorCS")])]})]});}
            var Q13;
            Q13=makeQuery(id+"F46.boolean.opBoolean","INTERSECT",EDGE,{"derivedFrom":[makeQuery(id+"F10.opFillet","BLEND_FACE",FACE,{"disambiguationData":[OSD([sQuery(id+"F0.wireOp",EDGE,"E0.top")])]}),makeQuery(id+"F46.opExtrude","SWEPT_FACE",FACE,{"disambiguationData":[OSD([sQuery(id+"F45.wireOp",EDGE,"E61.MirrorCS")])]})]});
            var Q14;
            Q14=makeQuery(id+"F46.boolean.opBoolean","INTERSECT",EDGE,{"derivedFrom":[makeQuery(id+"F10.opFillet","BLEND_FACE",FACE,{"disambiguationData":[OSD([sQuery(id+"F0.wireOp",EDGE,"E0.top")])]}),makeQuery(id+"F46.opExtrude","SWEPT_FACE",FACE,{"disambiguationData":[OSD([sQuery(id+"F45.wireOp",EDGE,"E63.MirrorCS")])]})]});
            var Q15;
            Q15=makeQuery(id+"F46.boolean.opBoolean","INTERSECT",EDGE,{"derivedFrom":[makeQuery(id+"F4.opShell","OFFSET_FACE",FACE,{"disambiguationData":[OSD([sQuery(id+"F0.wireOp",EDGE,"E0.top")])]}),makeQuery(id+"F46.opExtrude","CAP_FACE",FACE,{"disambiguationData":[OSD([sQuery(id+"F45.wireOp",EDGE,"E60.MirrorCS"),sQuery(id+"F45.wireOp",EDGE,"E61.MirrorCS"),sQuery(id+"F45.wireOp",EDGE,"E62.MirrorCS"),sQuery(id+"F45.wireOp",EDGE,"E63.MirrorCS")])],"isStart":false})]});
            fillet(context, id + "F47", {"entities" : qUnion([Q0, Q1, Q2, Q3, Q4, Q5, Q6, Q7, Q8, Q9, Q10, Q11, Q12, Q13, Q14, Q15]), "radius" : 0.5 * mm, "tangentPropagation" : true, "allowEdgeOverflow" : false});
        }
        {
            var Q0;
            Q0=makeQuery(id+"F1.opExtrude","CAP_FACE",FACE,{"disambiguationData":[OSD([sQuery(id+"F0.wireOp",EDGE,"E0.bottom"),sQuery(id+"F0.wireOp",EDGE,"E0.top"),sQuery(id+"F0.wireOp",EDGE,"E0.left"),sQuery(id+"F0.wireOp",EDGE,"E0.right")])],"isStart":false});
            var sketch = newSketch(context, id + "F48", { "sketchPlane" : qUnion([Q0])});
            skLineSegment(sketch, "E64", {"start": v(-28.58, 51.33) * mm, "end": v(-28.57, 8.89) * mm, "construction": true});
            skSolve(sketch);
        }
        {
            var Q0;
            Q0=makeQuery(id+"F1.opExtrude","SWEPT_FACE",FACE,{"disambiguationData":[OSD([sQuery(id+"F0.wireOp",EDGE,"E0.bottom")])]});
            var sketch = newSketch(context, id + "F49", { "sketchPlane" : qUnion([Q0])});
            skPoint(sketch, "E65.0", {"position": v(28.57, 7.6) * mm});
            skLineSegment(sketch, "E66.bottom", {"start": v(22.07, 8.18) * mm, "end": v(35.08, 8.18) * mm});
            skLineSegment(sketch, "E66.top", {"start": v(22.07, 4.8) * mm, "end": v(35.08, 4.8) * mm});
            skLineSegment(sketch, "E66.left", {"start": v(22.07, 8.18) * mm, "end": v(22.07, 4.8) * mm});
            skLineSegment(sketch, "E66.right", {"start": v(35.07, 8.18) * mm, "end": v(35.07, 4.8) * mm});
            skPoint(sketch, "E67", {"position": v(28.57, 8.18) * mm});
            skLineSegment(sketch, "E68", {"start": v(28.57, 7.6) * mm, "end": v(28.57, 8.9) * mm, "construction": true});
            skLineSegment(sketch, "E69", {"start": v(26.51, 8.8) * mm, "end": v(29.8, 8.8) * mm, "construction": true});
            skSolve(sketch);
        }
        {
            var Q0;
            Q0=qSketchRegion(id+"F49",true);
            extrude(context, id + "F50", {"entities" : qUnion([Q0]), "operationType" : NewBodyOperationType.REMOVE, "oppositeDirection" : true, "depth" : 1.6 * mm});
        }
        {
            var Q0;
            Q0=makeQuery(id+"F50.boolean.opBoolean","COPY",EDGE,{"derivedFrom":makeQuery(id+"F50.opExtrude","SWEPT_EDGE",EDGE,{"disambiguationData":[OSD([sQuery(id+"F49.wireOp",EDGE,"E66.top"),sQuery(id+"F49.wireOp",EDGE,"E66.left")])]})});
            var Q1;
            Q1=makeQuery(id+"F50.boolean.opBoolean","COPY",EDGE,{"derivedFrom":makeQuery(id+"F50.opExtrude","CAP_EDGE",EDGE,{"disambiguationData":[OSD([sQuery(id+"F49.wireOp",EDGE,"E66.top")])],"isStart":false})});
            var Q2;
            Q2=makeQuery(id+"F50.boolean.opBoolean","COPY",EDGE,{"derivedFrom":makeQuery(id+"F50.opExtrude","SWEPT_EDGE",EDGE,{"disambiguationData":[OSD([sQuery(id+"F49.wireOp",EDGE,"E66.top"),sQuery(id+"F49.wireOp",EDGE,"E66.right")])]})});
            var Q3;
            Q3=makeQuery(id+"F50.boolean.opBoolean","COPY",EDGE,{"derivedFrom":makeQuery(id+"F50.opExtrude","CAP_EDGE",EDGE,{"disambiguationData":[OSD([sQuery(id+"F49.wireOp",EDGE,"E66.right")])],"isStart":true})});
            fillet(context, id + "F51", {"entities" : qUnion([Q0, Q1, Q2, Q3]), "radius" : 0.5 * mm, "tangentPropagation" : true, "allowEdgeOverflow" : false});
        }
        {
            var Q0;
            Q0=makeQuery(id+"F1.opExtrude","SWEPT_FACE",FACE,{"disambiguationData":[OSD([sQuery(id+"F0.wireOp",EDGE,"E0.bottom")])]});
            var sketch = newSketch(context, id + "F52", { "sketchPlane" : qUnion([Q0])});
            skLineSegment(sketch, "E70.bottom", {"start": v(24.58, 9) * mm, "end": v(32.58, 9) * mm});
            skPoint(sketch, "E71.0", {"position": v(28.58, 7.6) * mm});
            skLineSegment(sketch, "E72", {"start": v(28.58, 7.6) * mm, "end": v(28.58, 11.52) * mm, "construction": true});
            skPoint(sketch, "E73", {"position": v(28.58, 9) * mm});
            skLineSegment(sketch, "E74", {"start": v(24.58, 9) * mm, "end": v(25.08, 7) * mm});
            skLineSegment(sketch, "E75", {"start": v(25.08, 7) * mm, "end": v(32.08, 7) * mm});
            skLineSegment(sketch, "E76", {"start": v(32.08, 7) * mm, "end": v(32.58, 9) * mm});
            skPoint(sketch, "E77", {"position": v(28.58, 7) * mm});
            skSolve(sketch);
        }
        {
            var Q0;
            Q0=qSketchRegion(id+"F52",true);
            extrude(context, id + "F53", {"entities" : qUnion([Q0]), "operationType" : NewBodyOperationType.REMOVE, "oppositeDirection" : true, "depth" : 25 * mm});
        }
    });
